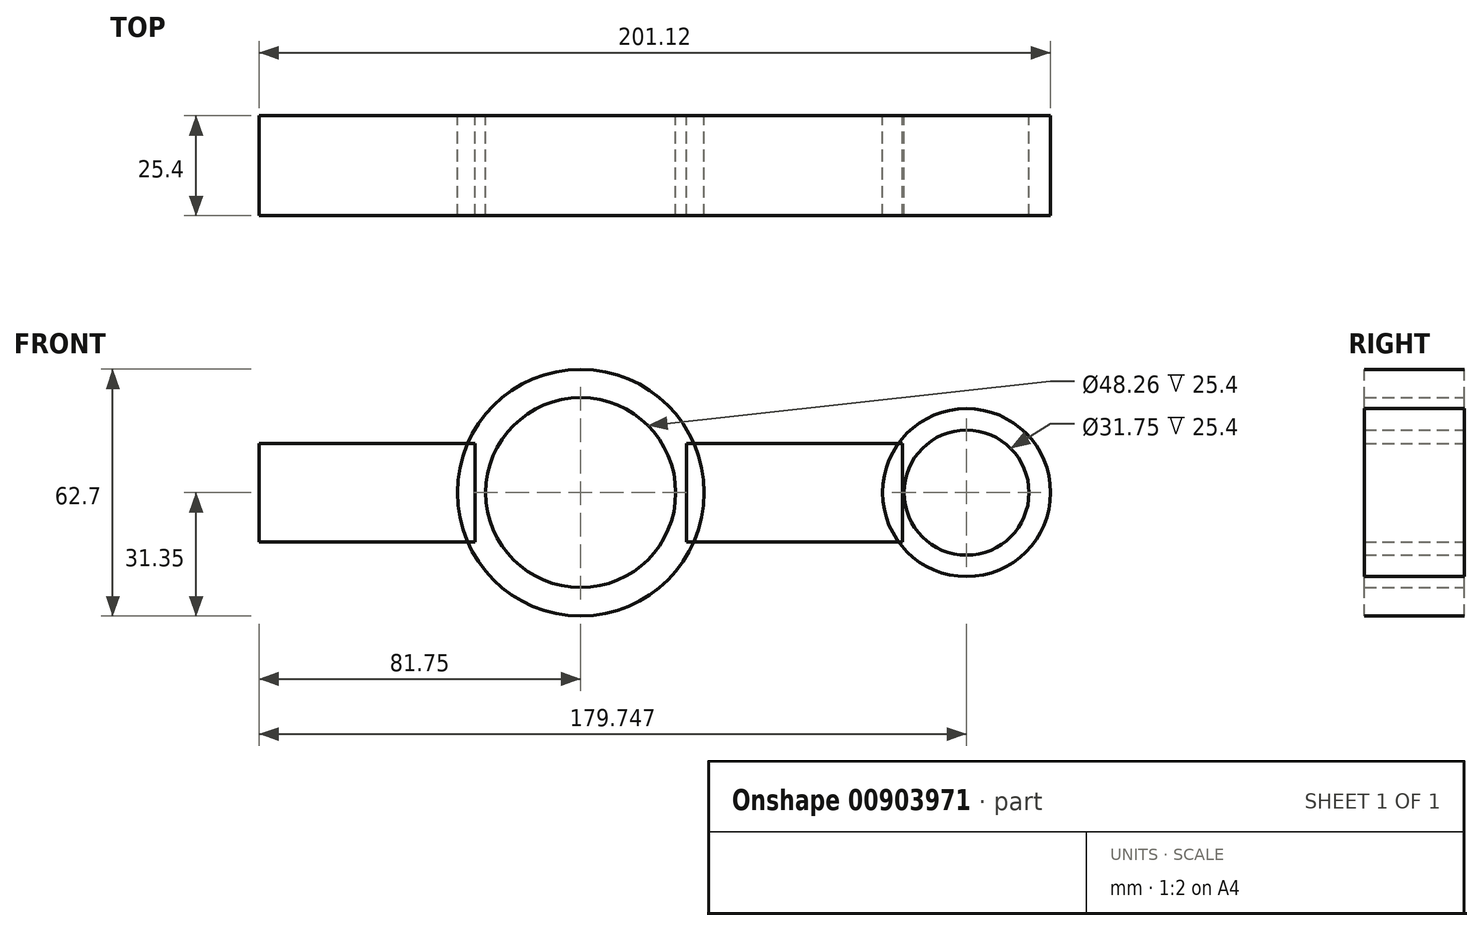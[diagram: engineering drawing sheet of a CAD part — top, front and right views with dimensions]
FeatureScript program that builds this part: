
annotation { "Feature Type Name" : "Feature", "Feature Type Description" : "" }
export const myFeature = defineFeature(function(context is Context, id is Id, definition is map)
    precondition{}
    {
        {
            var Q0;
            Q0=qCreatedBy(makeId("Front.planeOp"),FACE);
            var sketch = newSketch(context, id + "F0", { "sketchPlane" : qUnion([Q0])});
            skCircle(sketch, "E0", {"center": v(0, 0) * mm, "radius": 31.35 * mm});
            skCircle(sketch, "E1", {"center": v(0, 0) * mm, "radius": 24.13 * mm});
            skSolve(sketch);
        }
        {
            var Q0;
            Q0=qCreatedBy(makeId("Front.planeOp"),FACE);
            var sketch = newSketch(context, id + "F1", { "sketchPlane" : qUnion([Q0])});
            skCircle(sketch, "E2", {"center": v(98.03, 0) * mm, "radius": 21.34 * mm});
            skCircle(sketch, "E3.MirrorC", {"center": v(-98.03, 0) * mm, "radius": 21.34 * mm});
            skSolve(sketch);
        }
        {
            var Q0;
            Q0=qCreatedBy(makeId("Front.planeOp"),FACE);
            var sketch = newSketch(context, id + "F2", { "sketchPlane" : qUnion([Q0])});
            skCircle(sketch, "E4", {"center": v(-98, 0) * mm, "radius": 15.88 * mm});
            skCircle(sketch, "E5.MirrorC", {"center": v(98, 0) * mm, "radius": 15.88 * mm});
            skSolve(sketch);
        }
        {
            var Q0;
            Q0=qCreatedBy(makeId("Front.planeOp"),FACE);
            var sketch = newSketch(context, id + "F3", { "sketchPlane" : qUnion([Q0])});
            skLineSegment(sketch, "E6.bottom", {"start": v(26.89, -12.47) * mm, "end": v(81.75, -12.47) * mm});
            skLineSegment(sketch, "E6.top", {"start": v(26.89, 12.47) * mm, "end": v(81.75, 12.47) * mm});
            skLineSegment(sketch, "E6.left", {"start": v(26.89, -12.47) * mm, "end": v(26.89, 12.47) * mm});
            skLineSegment(sketch, "E6.right", {"start": v(81.75, -12.47) * mm, "end": v(81.75, 12.47) * mm});
            skPoint(sketch, "E6.middle", {"position": v(54.32, 0) * mm});
            skLineSegment(sketch, "E7.MirrorCS", {"start": v(-26.89, -12.47) * mm, "end": v(-81.75, -12.47) * mm});
            skLineSegment(sketch, "E8.MirrorCS", {"start": v(-26.89, -12.47) * mm, "end": v(-26.89, 12.47) * mm});
            skLineSegment(sketch, "E9.MirrorCS", {"start": v(-81.75, -12.47) * mm, "end": v(-81.75, 12.47) * mm});
            skLineSegment(sketch, "E10.MirrorCS", {"start": v(-26.89, 12.47) * mm, "end": v(-81.75, 12.47) * mm});
            skPoint(sketch, "E11.MirrorP", {"position": v(-54.32, 0) * mm});
            skSolve(sketch);
        }
        {
            var Q0;
            Q0=makeQuery(id+"F1.imprint","IMPRINT",FACE,{"disambiguationData":[TD([[makeQuery(id+"F1.imprint","IMPRINT",EDGE,{"derivedFrom":sQuery(id+"F1.wireOp",EDGE,"E3.MirrorC")}),-1.0]])]});
            var Q1;
            Q1=makeQuery(id+"F3.imprint","IMPRINT",FACE,{"disambiguationData":[TD([[makeQuery(id+"F3.imprint","IMPRINT",EDGE,{"derivedFrom":sQuery(id+"F3.wireOp",EDGE,"E7.MirrorCS")}),-1.0]])]});
            var Q2;
            Q2=makeQuery(id+"F0.imprint","IMPRINT",FACE,{"disambiguationData":[TD([[makeQuery(id+"F0.imprint","IMPRINT",EDGE,{"derivedFrom":sQuery(id+"F0.wireOp",EDGE,"E0")}),1.0]])]});
            var Q3;
            Q3=makeQuery(id+"F3.imprint","IMPRINT",FACE,{"disambiguationData":[TD([[makeQuery(id+"F3.imprint","IMPRINT",EDGE,{"derivedFrom":sQuery(id+"F3.wireOp",EDGE,"E6.bottom")}),1.0]])]});
            var Q4;
            Q4=makeQuery(id+"F1.imprint","IMPRINT",FACE,{"disambiguationData":[TD([[makeQuery(id+"F1.imprint","IMPRINT",EDGE,{"derivedFrom":sQuery(id+"F1.wireOp",EDGE,"E2")}),1.0]])]});
            extrude(context, id + "F4", {"entities" : qUnion([Q0, Q1, Q2, Q3, Q4]), "depth" : 25.4 * mm, "offsetDistance" : 25.4 * mm});
        }
        {
            var Q0;
            Q0=sQuery(id+"F2.wireOp",VERTEX,"E5.MirrorC.center");
            var Q1;
            Q1=sQuery(id+"F2.wireOp",VERTEX,"E4.center");
            var Q2;
            Q2=makeQuery(id+"F4.opExtrude","SWEPT_BODY",BODY,{"disambiguationData":[OSD([sQuery(id+"F1.wireOp",EDGE,"E2")])]});
            var Q3;
            Q3=makeQuery(id+"F4.opExtrude","SWEPT_BODY",BODY,{"disambiguationData":[OSD([sQuery(id+"F1.wireOp",EDGE,"E3.MirrorC")])]});
            hole(context, id + "F5", {"style" : HoleStyle.SIMPLE, "endStyle" : HoleEndStyle.THROUGH, "oppositeDirection" : true, "holeDiameter" : 31.75 * mm, "majorDiameter" : 6.35 * mm, "isTappedThrough" : true, "tappedDepth" : 12.7 * mm, "tapClearance" : 3, "locations" : qUnion([Q0, Q1]), "scope" : qUnion([Q2, Q3])});
        }
    });
